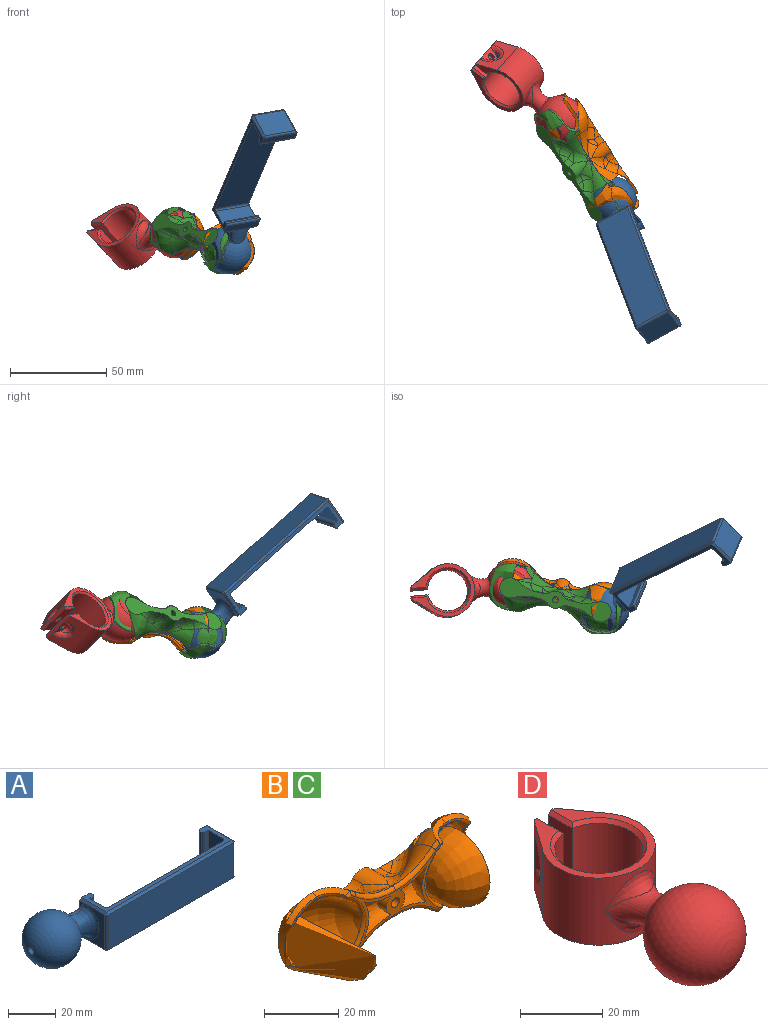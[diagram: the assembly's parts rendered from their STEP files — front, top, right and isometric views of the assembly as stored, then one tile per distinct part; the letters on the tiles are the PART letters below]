
ASSEMBLY  parts=4 mates=4
PART A: 46 faces, bbox 109.4x26.9x25.9 mm
  f0: plane 18.06x12.56mm, normal (-1,0,0), area 97.7mm2, adj f19,f29,f36,f45
  f1: plane 5.66x3.37mm, normal (-1,0,0), area 4.8mm2, adj f8,f20,f45
  f2: sphere r=12.5mm, area 1668.1mm2, adj f3,f18,f19,f20,f21,f22
  f3: plane 15x15mm, normal (0,0,-1), area 176.7mm2, adj f2
  f4: plane 5.66x3.37mm, normal (-1,0,0), area 4.8mm2, adj f8,f21,f36
  f5: plane 20x9mm, normal (1,0,0), area 180mm2, adj f6,f16,f17,f35
  f6: plane 20x2mm, normal (0,-1,0), area 40mm2, adj f5,f16,f17,f27
  f7: plane 20x1mm, normal (1,0,0), area 20mm2, adj f16,f17,f27,f28
  f8: plane 20x5mm, normal (0,1,0), area 99mm2, adj f1,f4,f16,f17,f18,f28,f36,f45
  f9: plane 74.75x18mm, normal (0,-1,0), area 1345.5mm2, adj f29,f30,f38,f43
  f10: plane 18x14mm, normal (1,0,0), area 252mm2, adj f30,f31,f40,f41
  f11: plane 20x4mm, normal (0,1,0), area 80mm2, adj f16,f17,f31,f32
  f12: plane 20x1mm, normal (-1,0,0), area 20mm2, adj f16,f17,f32,f33
  f13: plane 20x2mm, normal (0,-1,0), area 40mm2, adj f14,f16,f17,f33
  f14: plane 20x9mm, normal (-1,0,0), area 180mm2, adj f13,f16,f17,f34
  f15: plane 68.75x20mm, normal (0,1,0), area 1375mm2, adj f16,f17,f34,f35
  f16: plane 74.75x15mm, normal (0,0,1), area 219.1mm2, adj f5,f6,f7,f8,f11,f12,f13,f14
  f17: plane 74.75x15mm, normal (0,0,-1), area 219.1mm2, adj f5,f6,f7,f8,f11,f12,f13,f14
  f18: bspline ~14.32x8mm, area 52.9mm2, adj f2,f8,f20,f21
  f19: bspline ~18x13.55mm, area 213.3mm2, adj f0,f2,f20,f21
  f20: bspline ~11.31x8.33mm, area 31.4mm2, adj f1,f2,f18,f19
  f21: bspline ~11.31x8.33mm, area 31.4mm2, adj f2,f4,f18,f19
  f22: cone r=1.62mm half-angle=3deg, axis (-1,0,0), area 33.7mm2, adj f2,f23
  f23: sphere r=9mm, area 804.6mm2, adj f22,f24,f25
  f24: plane 8.83x8.83mm, normal (-1,0,0), area 60.2mm2, adj f23,f26
  f25: plane 12.45x12.45mm, normal (0,0,1), area 121.7mm2, adj f23
  f26: cone r=1.62mm half-angle=3deg, axis (-1,0,0), area 18.7mm2, adj f24
  f27: cylinder r=1mm len=20mm, axis (0,0,1), area 31.4mm2, adj f6,f7,f16,f17
  f28: cylinder r=1mm len=20mm, axis (0,0,-1), area 31.4mm2, adj f7,f8,f16,f17
  f29: cylinder r=1mm len=18mm, axis (0,0,-1), area 28.3mm2, adj f0,f9,f37,f44
  f30: cylinder r=1mm len=18mm, axis (0,0,-1), area 28.3mm2, adj f9,f10,f39,f42
  f31: cylinder r=1mm len=20mm, axis (0,0,-1), area 29.8mm2, adj f10,f11,f40,f41
  f32: cylinder r=1mm len=20mm, axis (0,0,-1), area 31.4mm2, adj f11,f12,f16,f17
  f33: cylinder r=1mm len=20mm, axis (0,0,1), area 31.4mm2, adj f12,f13,f16,f17
  f34: cylinder r=1mm len=20mm, axis (0,0,1), area 31.4mm2, adj f14,f15,f16,f17
  f35: cylinder r=1mm len=20mm, axis (0,0,1), area 31.4mm2, adj f5,f15,f16,f17
  f36: plane 15x1mm, normal (-0.71,0,0.71), area 21.2mm2, adj f0,f4,f8,f16,f37
  f37: cone r=1mm half-angle=45deg, axis (0,0,-1), area 1.1mm2, adj f29,f36,f38
  f38: plane 74.75x1mm, normal (0,-0.71,0.71), area 105.7mm2, adj f9,f16,f37,f39
  f39: cone r=1mm half-angle=45deg, axis (0,0,-1), area 1.1mm2, adj f30,f38,f40
  f40: plane 15.42x1.42mm, normal (0.71,0,0.71), area 20.9mm2, adj f10,f16,f31,f39
  f41: plane 15.42x1.42mm, normal (0.71,0,-0.71), area 20.9mm2, adj f10,f17,f31,f42
  f42: cone r=1mm half-angle=45deg, axis (0,0,1), area 1.1mm2, adj f30,f41,f43
  f43: plane 74.75x1mm, normal (0,-0.71,-0.71), area 105.7mm2, adj f9,f17,f42,f44
  f44: cone r=1mm half-angle=45deg, axis (0,0,1), area 1.1mm2, adj f29,f43,f45
  f45: plane 15x1mm, normal (-0.71,0,-0.71), area 21.2mm2, adj f0,f1,f8,f17,f44
PART B: 91 faces, bbox 72.1x19x28.1 mm
  f0: plane 59.78x10.4mm, normal (0,1,0), area 350.5mm2, adj f1,f2,f7,f13,f14,f15,f21,f23
  f1: plane 4.98x3.76mm, normal (0,0,1), area 10.1mm2, adj f0,f21,f22,f23
  f2: plane 4.98x3.76mm, normal (0,0,-1), area 10.1mm2, adj f0,f26,f27,f28
  f3: revolved ~14.78x8.77mm, area 71.8mm2, adj f7,f26,f28,f30,f44,f87
  f4: plane 9.69x5.17mm, normal (0,-1,0), area 6.9mm2, adj f10,f12,f33,f34,f39
  f5: revolved ~22.89x20.47mm, area 471.5mm2, adj f36,f37,f38,f39,f40,f41
  f6: revolved ~14.78x8.77mm, area 71.8mm2, adj f7,f21,f22,f25,f47,f81
  f7: revolved ~27.88x20.27mm, area 464.7mm2, adj f0,f3,f6,f21,f26,f31,f32,f33
  f8: plane 34.91x21.57mm, normal (0,-1,0), area 121.4mm2, adj f15,f16,f17,f18,f19,f20,f36,f53
  f9: plane 9.69x5.17mm, normal (0,-1,0), area 6.9mm2, adj f11,f12,f32,f33,f40
  f10: cylinder r=6.5mm len=6.41mm, axis (0,0,1), area 5.7mm2, adj f4,f35,f36,f37,f79
  f11: cylinder r=6.5mm len=6.41mm, axis (0,0,1), area 5.7mm2, adj f9,f31,f36,f38,f85
  f12: cylinder r=9mm len=12.45mm, axis (1,0,0), area 11.1mm2, adj f4,f9,f33,f39,f40,f41
  f13: cylinder r=4.5mm len=9.88mm, axis (0,1,0), area 50.1mm2, adj f0,f27,f30,f64,f67
  f14: cylinder r=4.5mm len=9.88mm, axis (0,1,0), area 50.1mm2, adj f0,f23,f25,f60,f62
  f15: cylinder r=1.5mm len=13mm, axis (0,1,0), area 122.5mm2, adj f0,f8
  f16: cylinder r=3.5mm len=5.74mm, axis (0,1,0), area 17mm2, adj f8,f17,f19,f20
  f17: plane 1.05x0.19mm, normal (-1,0,0), area 0.1mm2, adj f8,f16,f20
  f18: revolved ~11.81x5.9mm, area 58.7mm2, adj f8,f20
  f19: plane 1.05x0.19mm, normal (-1,0,0), area 0.1mm2, adj f8,f16,f20
  f20: revolved ~11.81x9.75mm, area 125.1mm2, adj f8,f16,f17,f18,f19
  f21: bspline ~12.49x9.13mm, area 25.5mm2, adj f0,f1,f6,f7,f22
  f22: bspline ~9.56x8.32mm, area 36.1mm2, adj f1,f6,f21,f24
  f23: cylinder r=5mm len=3.75mm, axis (0,1,0), area 15.3mm2, adj f0,f1,f14,f24
  f24: sphere r=5mm, area 20.4mm2, adj f22,f23,f25
  f25: bspline ~10.34x8.54mm, area 33.7mm2, adj f6,f14,f24,f62
  f26: bspline ~13.1x9.66mm, area 25.5mm2, adj f0,f2,f3,f7,f28
  f27: cylinder r=5mm len=3.75mm, axis (0,1,0), area 15.3mm2, adj f0,f2,f13,f29
  f28: bspline ~9.56x8.32mm, area 36.1mm2, adj f2,f3,f26,f29
  f29: sphere r=5mm, area 20.4mm2, adj f27,f28,f30
  f30: bspline ~9.38x7.96mm, area 33.7mm2, adj f3,f13,f29,f67
  f31: bspline ~7.76x6.42mm, area 16mm2, adj f7,f11,f32,f85,f86
  f32: bspline ~11.42x7.33mm, area 19.3mm2, adj f7,f9,f31,f33
  f33: bspline ~15.24x4.31mm, area 27mm2, adj f4,f7,f9,f12,f32,f34
  f34: bspline ~11.42x7.33mm, area 19.3mm2, adj f4,f7,f33,f35
  f35: bspline ~7.76x6.42mm, area 16mm2, adj f7,f10,f34,f79,f80
  f36: bspline ~21.95x7.72mm, area 36.2mm2, adj f5,f8,f10,f11,f37,f38,f79,f85
  f37: bspline ~8.5x6.98mm, area 9.1mm2, adj f5,f10,f36,f39
  f38: bspline ~8.5x6.98mm, area 9.1mm2, adj f5,f11,f36,f40
  f39: bspline ~10.93x5.33mm, area 10mm2, adj f4,f5,f12,f37,f41
  f40: bspline ~10.93x5.33mm, area 10mm2, adj f5,f9,f12,f38,f41
  f41: bspline ~14.29x3.88mm, area 9.7mm2, adj f5,f12,f39,f40
  f42: plane 4.98x3.76mm, normal (0,0,1), area 10.1mm2, adj f0,f58,f59,f60
  f43: plane 4.98x3.76mm, normal (0,0,-1), area 10.1mm2, adj f0,f63,f64,f65
  f44: revolved ~14.78x8.77mm, area 71.8mm2, adj f3,f48,f63,f65,f67,f88
  f45: plane 9.69x5.17mm, normal (0,-1,0), area 6.9mm2, adj f50,f52,f70,f71,f76
  f46: revolved ~22.89x20.47mm, area 471.5mm2, adj f73,f74,f75,f76,f77,f78
  f47: revolved ~14.78x8.77mm, area 71.8mm2, adj f6,f48,f58,f59,f62,f82
  f48: revolved ~27.88x20.27mm, area 464.6mm2, adj f0,f44,f47,f58,f63,f68,f69,f70
  f49: plane 9.69x5.17mm, normal (0,-1,0), area 6.9mm2, adj f51,f52,f69,f70,f77
  f50: cylinder r=6.5mm len=6.41mm, axis (0,0,1), area 5.7mm2, adj f45,f72,f73,f74,f83
  f51: cylinder r=6.5mm len=6.41mm, axis (0,0,1), area 5.7mm2, adj f49,f68,f73,f75,f90
  f52: cylinder r=9mm len=12.45mm, axis (-1,0,0), area 11.1mm2, adj f45,f49,f70,f76,f77,f78
  f53: cylinder r=3.5mm len=5.74mm, axis (0,1,0), area 17mm2, adj f8,f54,f56,f57
  f54: plane 1.05x0.19mm, normal (1,0,0), area 0.1mm2, adj f8,f53,f57
  f55: revolved ~11.81x5.9mm, area 58.7mm2, adj f8,f57
  f56: plane 1.05x0.19mm, normal (1,0,0), area 0.1mm2, adj f8,f53,f57
  f57: revolved ~11.81x9.75mm, area 125.1mm2, adj f8,f53,f54,f55,f56
  f58: bspline ~13.1x9.66mm, area 25.5mm2, adj f0,f42,f47,f48,f59
  f59: bspline ~9.56x8.32mm, area 36.1mm2, adj f42,f47,f58,f61
  f60: cylinder r=5mm len=3.75mm, axis (0,1,0), area 15.3mm2, adj f0,f14,f42,f61
  f61: sphere r=5mm, area 16.3mm2, adj f59,f60,f62
  f62: bspline ~10.05x8.54mm, area 33.7mm2, adj f14,f25,f47,f61
  f63: bspline ~12.49x9.13mm, area 25.5mm2, adj f0,f43,f44,f48,f65
  f64: cylinder r=5mm len=3.75mm, axis (0,1,0), area 15.3mm2, adj f0,f13,f43,f66
  f65: bspline ~9.56x8.32mm, area 36.1mm2, adj f43,f44,f63,f66
  f66: sphere r=5mm, area 20.4mm2, adj f64,f65,f67
  f67: bspline ~9.72x7.96mm, area 33.7mm2, adj f13,f30,f44,f66
  f68: bspline ~7.97x7.55mm, area 16mm2, adj f48,f51,f69,f89,f90
  f69: bspline ~11.42x7.33mm, area 19.3mm2, adj f48,f49,f68,f70
  f70: bspline ~15.99x4.66mm, area 27mm2, adj f45,f48,f49,f52,f69,f71
  f71: bspline ~10.29x5.59mm, area 19.3mm2, adj f45,f48,f70,f72
  f72: bspline ~7.76x6.42mm, area 16mm2, adj f48,f50,f71,f83,f84
  f73: bspline ~21.95x7.72mm, area 36.2mm2, adj f8,f46,f50,f51,f74,f75,f83,f90
  f74: bspline ~8.5x6.98mm, area 9.1mm2, adj f46,f50,f73,f76
  f75: bspline ~8.5x6.98mm, area 9.1mm2, adj f46,f51,f73,f77
  f76: bspline ~10.93x5.33mm, area 10mm2, adj f45,f46,f52,f74,f78
  f77: bspline ~10.93x5.33mm, area 10mm2, adj f46,f49,f52,f75,f78
  f78: bspline ~14.29x3.88mm, area 9.7mm2, adj f46,f52,f76,f77
  f79: bspline ~2.26x1.82mm, area 1.9mm2, adj f8,f10,f35,f36,f80
  f80: bspline ~3.63x3.01mm, area 3.6mm2, adj f7,f8,f35,f79,f81
  f81: bspline ~21.28x7mm, area 28.5mm2, adj f6,f7,f8,f80,f82
  f82: bspline ~21.28x7mm, area 28.5mm2, adj f8,f47,f48,f81,f84
  f83: bspline ~2.41x1.9mm, area 1.9mm2, adj f8,f50,f72,f73,f84
  f84: bspline ~3.63x3.01mm, area 3.6mm2, adj f8,f48,f72,f82,f83
  f85: bspline ~2.26x1.82mm, area 1.9mm2, adj f8,f11,f31,f36,f86
  f86: bspline ~3.63x3.01mm, area 3.6mm2, adj f7,f8,f31,f85,f87
  f87: bspline ~21.28x7mm, area 28.5mm2, adj f3,f7,f8,f86,f88
  f88: bspline ~21.28x7mm, area 28.5mm2, adj f8,f44,f48,f87,f89
  f89: bspline ~3.63x3.01mm, area 3.6mm2, adj f8,f48,f68,f88,f90
  f90: bspline ~2.41x1.9mm, area 1.9mm2, adj f8,f51,f68,f73,f89
PART C: same geometry as B
PART D: 32 faces, bbox 27.5x64.4x25 mm
  f0: cylinder r=13.75mm len=27.5mm, axis (0,0,-1), area 1205.2mm2, adj f1,f5,f6,f26,f27,f28
  f1: bspline ~16.85x8.55mm, area 0mm2, adj f0,f2
  f2: revolved ~16.85x16.85mm, area 232.1mm2, adj f1,f3,f5
  f3: sphere r=12.5mm, area 1676.4mm2, adj f2,f4
  f4: plane 15x15mm, normal (0,0,-1), area 176.7mm2, adj f3
  f5: bspline ~16.85x8.55mm, area 0mm2, adj f0,f2
  f6: plane 20x10.76mm, normal (-0.81,0.58,0), area 162.4mm2, adj f0,f7,f25,f26,f28
  f7: bspline ~12.5x8.2mm, area 68.7mm2, adj f6,f8,f9
  f8: cylinder r=3.25mm len=6.27mm, axis (1,0,0), area 0mm2, adj f7,f9
  f9: plane 12x6.75mm, normal (-1,0,0), area 37mm2, adj f7,f8,f10,f25
  f10: cylinder r=1.62mm len=3.25mm, axis (1,0,0), area 20.4mm2, adj f9,f11
  f11: plane 18x8.11mm, normal (1,0,0), area 137.6mm2, adj f10,f12,f23,f24,f25
  f12: plane 8.14x1.03mm, normal (0.71,0,0.71), area 10.9mm2, adj f11,f13,f25,f26
  f13: cone r=10.75mm half-angle=45deg, axis (0,0,1), area 94.3mm2, adj f12,f14,f24,f26
  f14: plane 8.14x1.03mm, normal (-0.71,0,0.71), area 10.9mm2, adj f13,f15,f22,f26
  f15: plane 18x8.11mm, normal (-1,0,0), area 137.6mm2, adj f14,f16,f18,f22,f24
  f16: plane 8.14x1.03mm, normal (-0.71,0,-0.71), area 10.9mm2, adj f15,f17,f22,f28
  f17: cone r=11.75mm half-angle=45deg, axis (0,0,-1), area 94.3mm2, adj f16,f23,f24,f28
  f18: cylinder r=1.62mm len=3.25mm, axis (1,0,0), area 20.4mm2, adj f15,f19
  f19: plane 12x6.75mm, normal (1,0,0), area 37mm2, adj f18,f20,f21,f22
  f20: cylinder r=3.25mm len=6.27mm, axis (-1,0,0), area 0mm2, adj f19,f21
  f21: bspline ~12.5x8.2mm, area 68.7mm2, adj f19,f20,f27
  f22: plane 20x2mm, normal (0,1,0), area 39mm2, adj f14,f15,f16,f19,f26,f27,f28
  f23: plane 8.14x1.03mm, normal (0.71,0,-0.71), area 10.9mm2, adj f11,f17,f25,f28
  f24: cylinder r=10.75mm len=21.5mm, axis (0,0,-1), area 1161.6mm2, adj f11,f13,f15,f17
  f25: plane 20x2mm, normal (0,1,0), area 39mm2, adj f6,f9,f11,f12,f23,f26,f28
  f26: plane 32.5x27.5mm, normal (0,0,1), area 192.5mm2, adj f0,f6,f12,f13,f14,f22,f25,f27
  f27: plane 20x10.76mm, normal (0.81,0.58,0), area 162.4mm2, adj f0,f21,f22,f26,f28
  f28: plane 32.5x27.5mm, normal (0,0,-1), area 192.5mm2, adj f0,f6,f16,f17,f22,f23,f25,f27
  f29: sphere r=9mm, area 811.2mm2, adj f30,f31
  f30: plane 8.83x8.83mm, normal (0,-1,0), area 61.2mm2, adj f29
  f31: plane 12.45x12.45mm, normal (0,0,1), area 121.7mm2, adj f29
PLACE A rot(axis=(-0.73,0.14,-0.67),122.9deg) t=(-5.28,-52.34,-13.01)mm fixed
PLACE B rot(axis=(-0.47,-0.88,0.02),168.2deg) t=(-25.58,-16.19,-23.5)mm
PLACE C rot(axis=(0.22,0.21,0.95),127.7deg) t=(-24.08,-15.1,-24.13)mm
PLACE D rot(axis=(-0.42,0.89,0.19),131deg) t=(-63.65,26.58,-20.89)mm
MATE ball B.f3 <-> D.f3  axis (0.54,-0.83,-0.16) through (-38.33,5.32,-19.53)mm
MATE ball D.f3 <-> C.f3  axis (0.53,0.6,-0.6) through (-38.33,5.32,-19.53)mm
MATE ball C.f57 <-> A.f2  axis (-0.54,0.83,0.16) through (-11.18,-36.59,-27.73)mm
MATE ball B.f57 <-> A.f2  axis (-0.54,0.83,0.16) through (-11.18,-36.59,-27.73)mm
